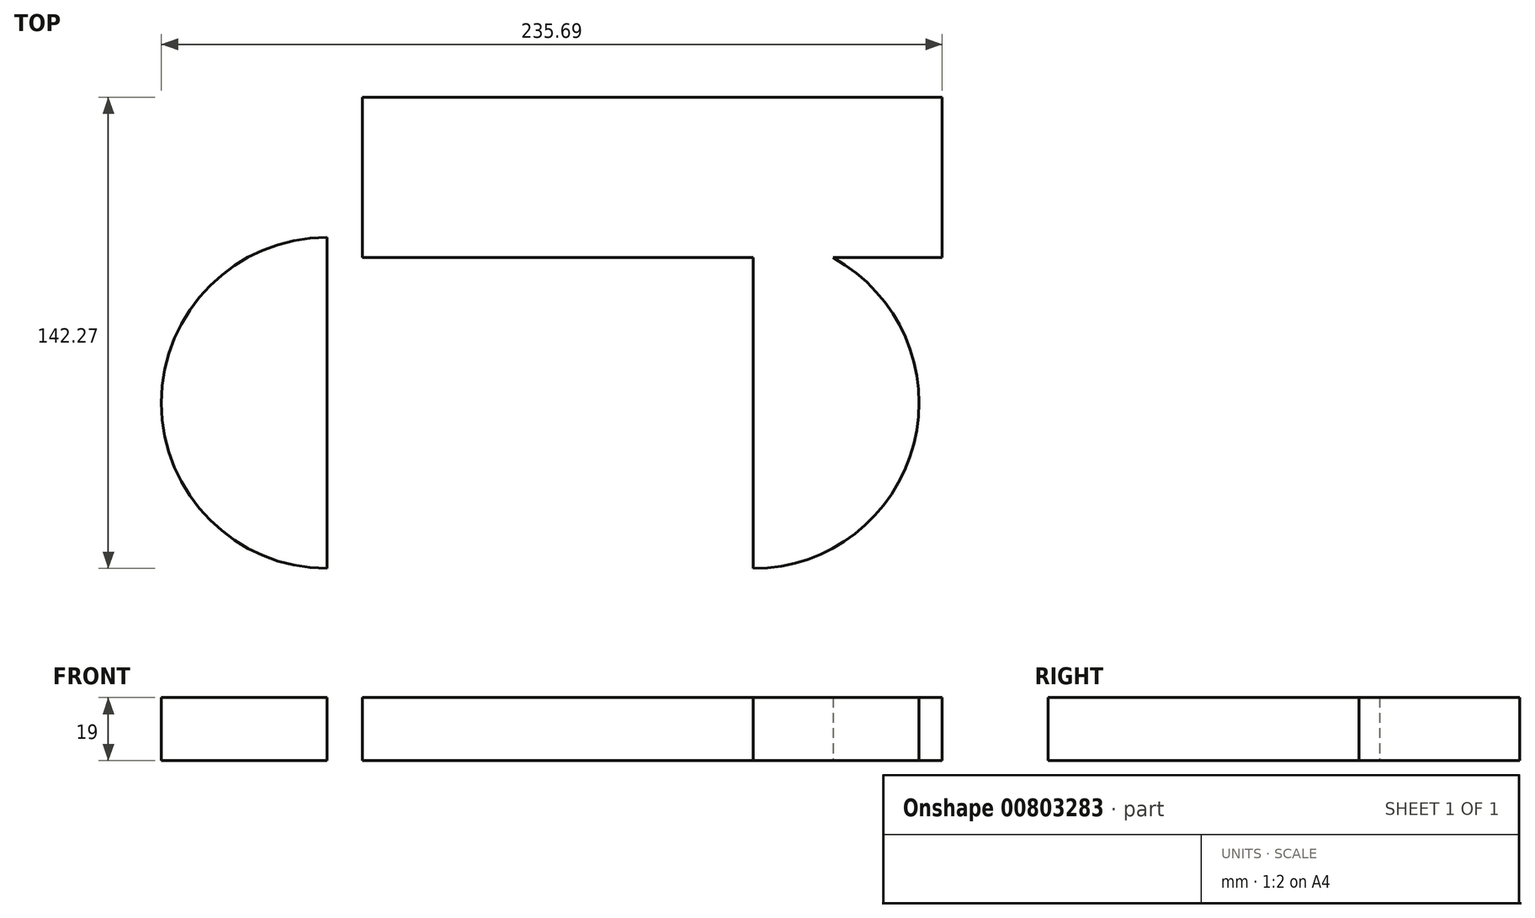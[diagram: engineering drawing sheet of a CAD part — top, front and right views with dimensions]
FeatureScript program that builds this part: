
annotation { "Feature Type Name" : "Feature", "Feature Type Description" : "" }
export const myFeature = defineFeature(function(context is Context, id is Id, definition is map)
    precondition{}
    {
        {
            var Q0;
            Q0=qCreatedBy(makeId("Top.planeOp"),FACE);
            var sketch = newSketch(context, id + "F0", { "sketchPlane" : qUnion([Q0])});
            skArc(sketch, "E0", {"start": v(0, -50) * mm, "mid": v(50, 0) * mm, "end": v(0, 50) * mm});
            skArc(sketch, "E1", {"start": v(-128.68, 50) * mm, "mid": v(-178.68, 0) * mm, "end": v(-128.68, -50) * mm});
            skLineSegment(sketch, "E2.bottom", {"start": v(-118, 92.27) * mm, "end": v(57, 92.27) * mm});
            skLineSegment(sketch, "E2.top", {"start": v(-118, 43.84) * mm, "end": v(57, 43.84) * mm});
            skLineSegment(sketch, "E2.left", {"start": v(-118, 92.27) * mm, "end": v(-118, 43.84) * mm});
            skLineSegment(sketch, "E2.right", {"start": v(57, 92.27) * mm, "end": v(57, 43.84) * mm});
            skLineSegment(sketch, "E3", {"start": v(-128.68, -50) * mm, "end": v(-128.68, 50) * mm});
            skLineSegment(sketch, "E4", {"start": v(0, -50) * mm, "end": v(0, 50) * mm});
            skSolve(sketch);
        }
        {
            var Q0;
            Q0=makeQuery(id+"F0.imprint","IMPRINT",FACE,{"disambiguationData":[TD([[makeQuery(id+"F0.imprint","IMPRINT",EDGE,{"derivedFrom":sQuery(id+"F0.wireOp",EDGE,"E1")}),1.0]])]});
            var Q1;
            Q1=makeQuery(id+"F0.imprint","IMPRINT",FACE,{"disambiguationData":[TD([[makeQuery(id+"F0.imprint","IMPRINT",EDGE,{"derivedFrom":sQuery(id+"F0.wireOp",EDGE,"E2.bottom")}),-1.0]])]});
            var Q2;
            Q2=makeQuery(id+"F0.imprint","IMPRINT",FACE,{"disambiguationData":[TD([[makeQuery(id+"F0.imprint","IMPRINT",EDGE,{"derivedFrom":sQuery(id+"F0.wireOp",EDGE,"E0")}),1.0]])]});
            extrude(context, id + "F1", {"entities" : qUnion([Q0, Q1, Q2]), "depth" : 19 * mm, "offsetDistance" : 25 * mm});
        }
    });
